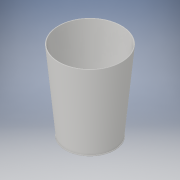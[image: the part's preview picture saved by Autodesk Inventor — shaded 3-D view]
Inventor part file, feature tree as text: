
AUTODESK INVENTOR PART (.ipt)
format: ipt  version: 2017 (Build 210142000, 142)  size: 148,480 bytes
history: native  units: in
note: dims shown in document units (in); Inventor stores cm internally (conversion verified against a paired STEP export)
features: sketch x3, other x2, revolve x1
ambient origin geometry x8: Origin, YZ Plane, XZ Plane, XY Plane, X Axis, Y Axis, Z Axis, Center Point
bodies: Solid1 (feature_tree)
feature tree (6):
  other  "bace"
  other  "walls"
  revolve  "Revolution3"  [1 undecoded]
  sketch  "Sketch1"  dims[d0=0.3333in d1=0.012in]
  sketch  "Sketch2"  dims[d2=0.3333in]
  sketch  "Sketch3"  dims[d3=0.3333in d4=90.0deg d5=1.0833in d6=0.012in d7=0.012in d8=90.0deg d10=0.006in d11=90.0deg]
note: 1 required parameter value undecoded (feature->parameter linkage not recoverable at this tier; creation-order binding heuristic only, values carry confidence <= 0.55)
